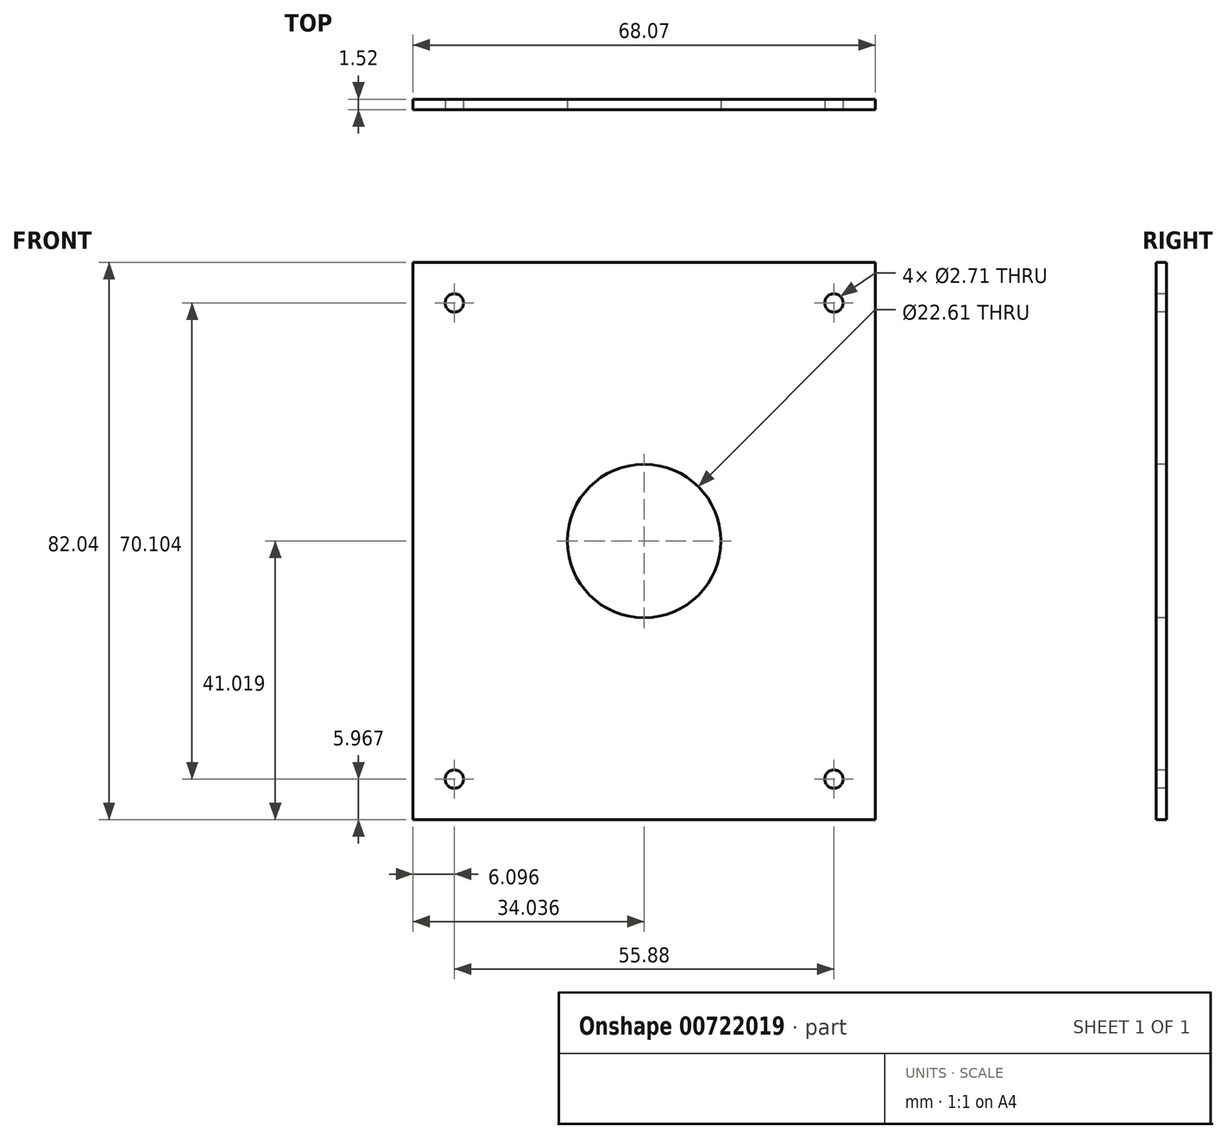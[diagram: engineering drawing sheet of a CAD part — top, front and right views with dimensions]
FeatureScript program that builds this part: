
annotation { "Feature Type Name" : "Feature", "Feature Type Description" : "" }
export const myFeature = defineFeature(function(context is Context, id is Id, definition is map)
    precondition{}
    {
        {
            var Q0;
            Q0=qCreatedBy(makeId("Front.planeOp"),FACE);
            var sketch = newSketch(context, id + "F0", { "sketchPlane" : qUnion([Q0])});
            skLineSegment(sketch, "E0.bottom", {"start": v(0, 0) * mm, "end": v(68.07, 0) * mm});
            skLineSegment(sketch, "E0.top", {"start": v(0, -82.04) * mm, "end": v(68.07, -82.04) * mm});
            skLineSegment(sketch, "E0.left", {"start": v(0, 0) * mm, "end": v(0, -82.04) * mm});
            skLineSegment(sketch, "E0.right", {"start": v(68.07, 0) * mm, "end": v(68.07, -82.04) * mm});
            skSolve(sketch);
        }
        {
            var Q0;
            Q0=qSketchRegion(id+"F0",true);
            extrude(context, id + "F1", {"entities" : qUnion([Q0]), "depth" : 1.52 * mm, "offsetDistance" : 25.4 * mm});
        }
        {
            var Q0;
            Q0=makeQuery(id+"F1.opExtrude","CAP_FACE",FACE,{"disambiguationData":[OSD([sQuery(id+"F0.wireOp",EDGE,"E0.bottom"),sQuery(id+"F0.wireOp",EDGE,"E0.top"),sQuery(id+"F0.wireOp",EDGE,"E0.left"),sQuery(id+"F0.wireOp",EDGE,"E0.right")])],"isStart":false});
            var sketch = newSketch(context, id + "F2", { "sketchPlane" : qUnion([Q0])});
            skPoint(sketch, "E1", {"position": v(6.1, -5.97) * mm});
            skPoint(sketch, "E2", {"position": v(61.98, -5.97) * mm});
            skPoint(sketch, "E3", {"position": v(61.98, -76.07) * mm});
            skPoint(sketch, "E4", {"position": v(6.1, -76.07) * mm});
            skLineSegment(sketch, "E5", {"start": v(34.04, 0) * mm, "end": v(34.04, -82.04) * mm, "construction": true});
            skLineSegment(sketch, "E6", {"start": v(68.07, -41.02) * mm, "end": v(0, -41.02) * mm, "construction": true});
            skSolve(sketch);
        }
        {
            var Q0;
            Q0=sQuery(id+"F2.wireOp",VERTEX,"E1");
            var Q1;
            Q1=sQuery(id+"F2.wireOp",VERTEX,"E2");
            var Q2;
            Q2=sQuery(id+"F2.wireOp",VERTEX,"E3");
            var Q3;
            Q3=sQuery(id+"F2.wireOp",VERTEX,"E4");
            var Q4;
            Q4=makeQuery(id+"F1.opExtrude","SWEPT_BODY",BODY,{"disambiguationData":[OSD([sQuery(id+"F0.wireOp",EDGE,"E0.bottom"),sQuery(id+"F0.wireOp",EDGE,"E0.top"),sQuery(id+"F0.wireOp",EDGE,"E0.left"),sQuery(id+"F0.wireOp",EDGE,"E0.right")])]});
            hole(context, id + "F3", {"style" : HoleStyle.SIMPLE, "endStyle" : HoleEndStyle.THROUGH, "standardTappedOrClearance" : lookupTablePath({ "standard" : "ANSI", "engagement" : "75%", "pitch" : "32 tpi", "size" : "#6", "type" : "Tapped" }), "standardBlindInLast" : lookupTablePath({ "standard" : "ANSI", "engagement" : "75%", "pitch" : "32 tpi", "size" : "#6", "type" : "Tapped" }), "holeDiameter" : 2.7 * mm, "majorDiameter" : 3.5 * mm, "showTappedDepth" : true, "isTappedThrough" : true, "tappedDepth" : 10.32 * mm, "tapClearance" : 3, "startFromSketch" : true, "locations" : qUnion([Q0, Q1, Q2, Q3]), "scope" : qUnion([Q4])});
        }
        {
            var Q0;
            Q0=makeQuery(id+"F1.opExtrude","CAP_FACE",FACE,{"disambiguationData":[OSD([sQuery(id+"F0.wireOp",EDGE,"E0.bottom"),sQuery(id+"F0.wireOp",EDGE,"E0.top"),sQuery(id+"F0.wireOp",EDGE,"E0.left"),sQuery(id+"F0.wireOp",EDGE,"E0.right")])],"isStart":false});
            var sketch = newSketch(context, id + "F4", { "sketchPlane" : qUnion([Q0])});
            skCircle(sketch, "E7", {"center": v(34.04, -41.02) * mm, "radius": 11.3 * mm});
            skLineSegment(sketch, "E8", {"start": v(34.04, 0) * mm, "end": v(34.04, -82.04) * mm, "construction": true});
            skLineSegment(sketch, "E9", {"start": v(68.07, -41.02) * mm, "end": v(0, -41.02) * mm, "construction": true});
            skSolve(sketch);
        }
        {
            var Q0;
            Q0 = qSketchRegion(id + "F4", true);
            extrude(context, id + "F5", {"entities" : qUnion([Q0]), "operationType" : NewBodyOperationType.REMOVE, "endBound" : BoundingType.THROUGH_ALL, "oppositeDirection" : true, "depth" : 25.4 * mm, "offsetDistance" : 25.4 * mm});
        }
    });
